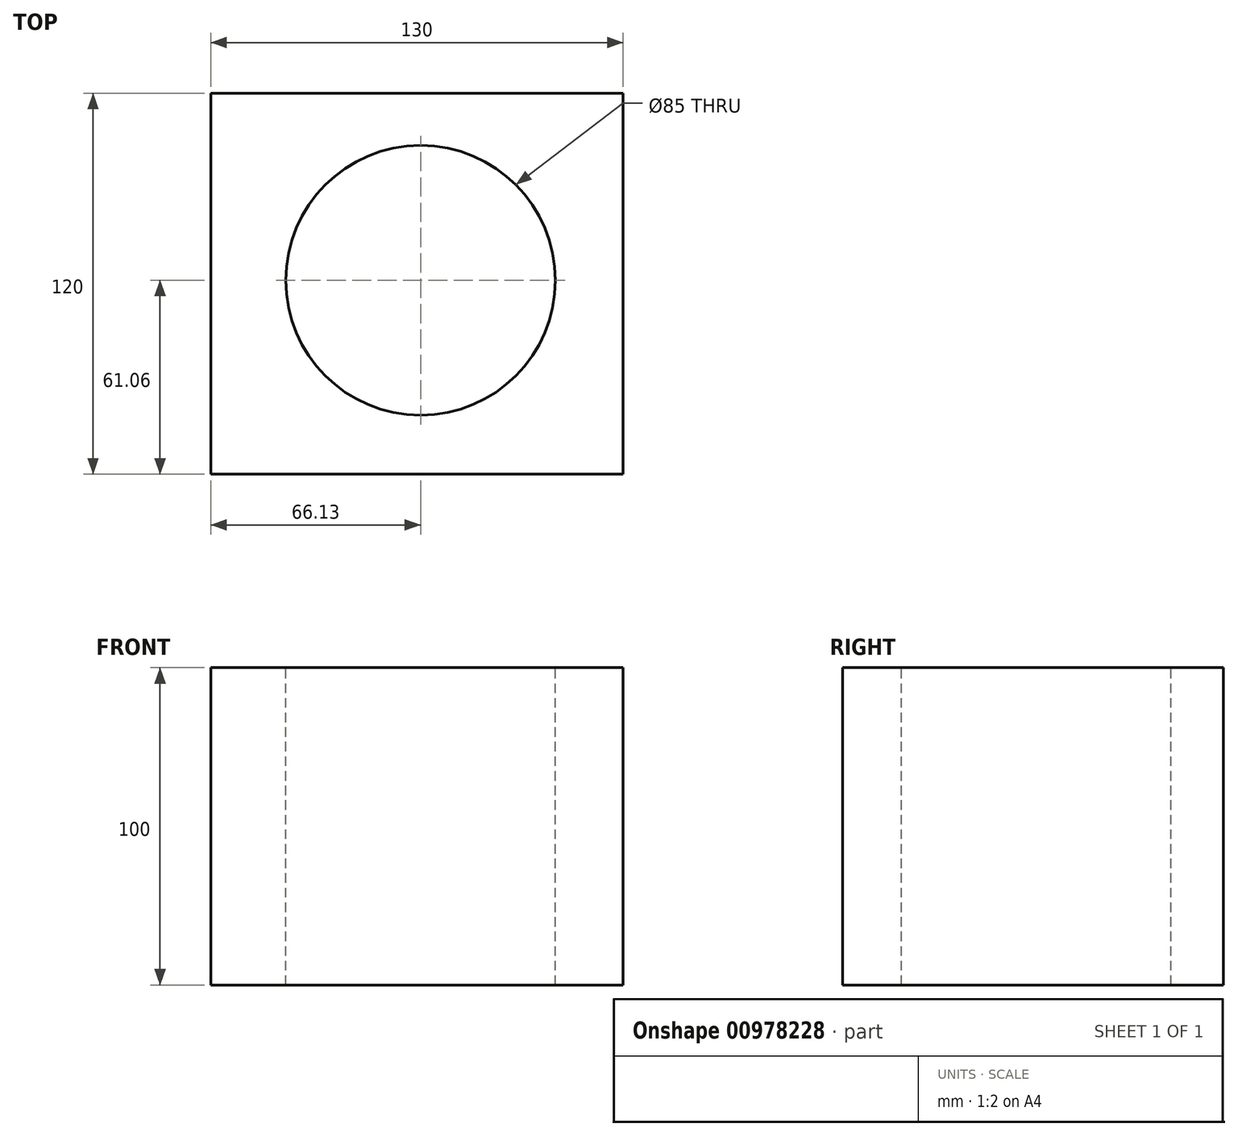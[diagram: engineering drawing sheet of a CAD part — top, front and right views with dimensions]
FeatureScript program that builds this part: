
annotation { "Feature Type Name" : "Feature", "Feature Type Description" : "" }
export const myFeature = defineFeature(function(context is Context, id is Id, definition is map)
    precondition{}
    {
        {
            var Q0;
            Q0=qCreatedBy(makeId("Top.planeOp"),FACE);
            var sketch = newSketch(context, id + "F0", { "sketchPlane" : qUnion([Q0])});
            skLineSegment(sketch, "E0.bottom", {"start": v(-66.13, 58.94) * mm, "end": v(63.87, 58.94) * mm});
            skLineSegment(sketch, "E0.top", {"start": v(-66.13, -61.06) * mm, "end": v(63.87, -61.06) * mm});
            skLineSegment(sketch, "E0.left", {"start": v(-66.13, 58.94) * mm, "end": v(-66.13, -61.06) * mm});
            skLineSegment(sketch, "E0.right", {"start": v(63.87, 58.94) * mm, "end": v(63.87, -61.06) * mm});
            skSolve(sketch);
        }
        {
            var Q0;
            Q0=makeQuery(id+"F0.imprint","IMPRINT",FACE,{"disambiguationData":[TD([[makeQuery(id+"F0.imprint","IMPRINT",EDGE,{"derivedFrom":sQuery(id+"F0.wireOp",EDGE,"E0.bottom")}),-1.0]])]});
            extrude(context, id + "F1", {"entities" : qUnion([Q0]), "depth" : 50 * mm, "offsetDistance" : 25 * mm});
        }
        {
            var Q0;
            Q0=makeQuery(id+"F1.opExtrude","SWEPT_BODY",BODY,{"disambiguationData":[OSD([sQuery(id+"F0.wireOp",EDGE,"E0.bottom"),sQuery(id+"F0.wireOp",EDGE,"E0.top"),sQuery(id+"F0.wireOp",EDGE,"E0.left"),sQuery(id+"F0.wireOp",EDGE,"E0.right")])]});
            var Q1;
            Q1=makeQuery(id+"F1.opExtrude","CAP_FACE",FACE,{"disambiguationData":[OSD([sQuery(id+"F0.wireOp",EDGE,"E0.bottom"),sQuery(id+"F0.wireOp",EDGE,"E0.top"),sQuery(id+"F0.wireOp",EDGE,"E0.left"),sQuery(id+"F0.wireOp",EDGE,"E0.right")])],"isStart":true});
            mirror(context, id + "F2", {"operationType" : NewBodyOperationType.ADD, "entities" : qUnion([Q0]), "mirrorPlane" : qUnion([Q1])});
        }
        {
            var Q0;
            Q0=makeQuery(id+"F1.opExtrude","CAP_FACE",FACE,{"disambiguationData":[OSD([sQuery(id+"F0.wireOp",EDGE,"E0.bottom"),sQuery(id+"F0.wireOp",EDGE,"E0.top"),sQuery(id+"F0.wireOp",EDGE,"E0.left"),sQuery(id+"F0.wireOp",EDGE,"E0.right")])],"isStart":false});
            var sketch = newSketch(context, id + "F3", { "sketchPlane" : qUnion([Q0])});
            skCircle(sketch, "E1", {"center": v(0, 0) * mm, "radius": 47.5 * mm});
            skSolve(sketch);
        }
        {
            var Q0;
            Q0=makeQuery(id+"F3.imprint","IMPRINT",FACE,{"disambiguationData":[TD([[makeQuery(id+"F3.imprint","IMPRINT",EDGE,{"derivedFrom":sQuery(id+"F3.wireOp",EDGE,"E1")}),-1.0]])]});
            var sketch = newSketch(context, id + "F4", { "sketchPlane" : qUnion([Q0])});
            skCircle(sketch, "E2", {"center": v(0, 0) * mm, "radius": 42.5 * mm});
            skSolve(sketch);
        }
        {
            var Q0;
            Q0 = qSketchRegion(id + "F4", true);
            extrude(context, id + "F5", {"entities" : qUnion([Q0]), "operationType" : NewBodyOperationType.REMOVE, "oppositeDirection" : true, "depth" : 100 * mm, "offsetDistance" : 25 * mm});
        }
    });
